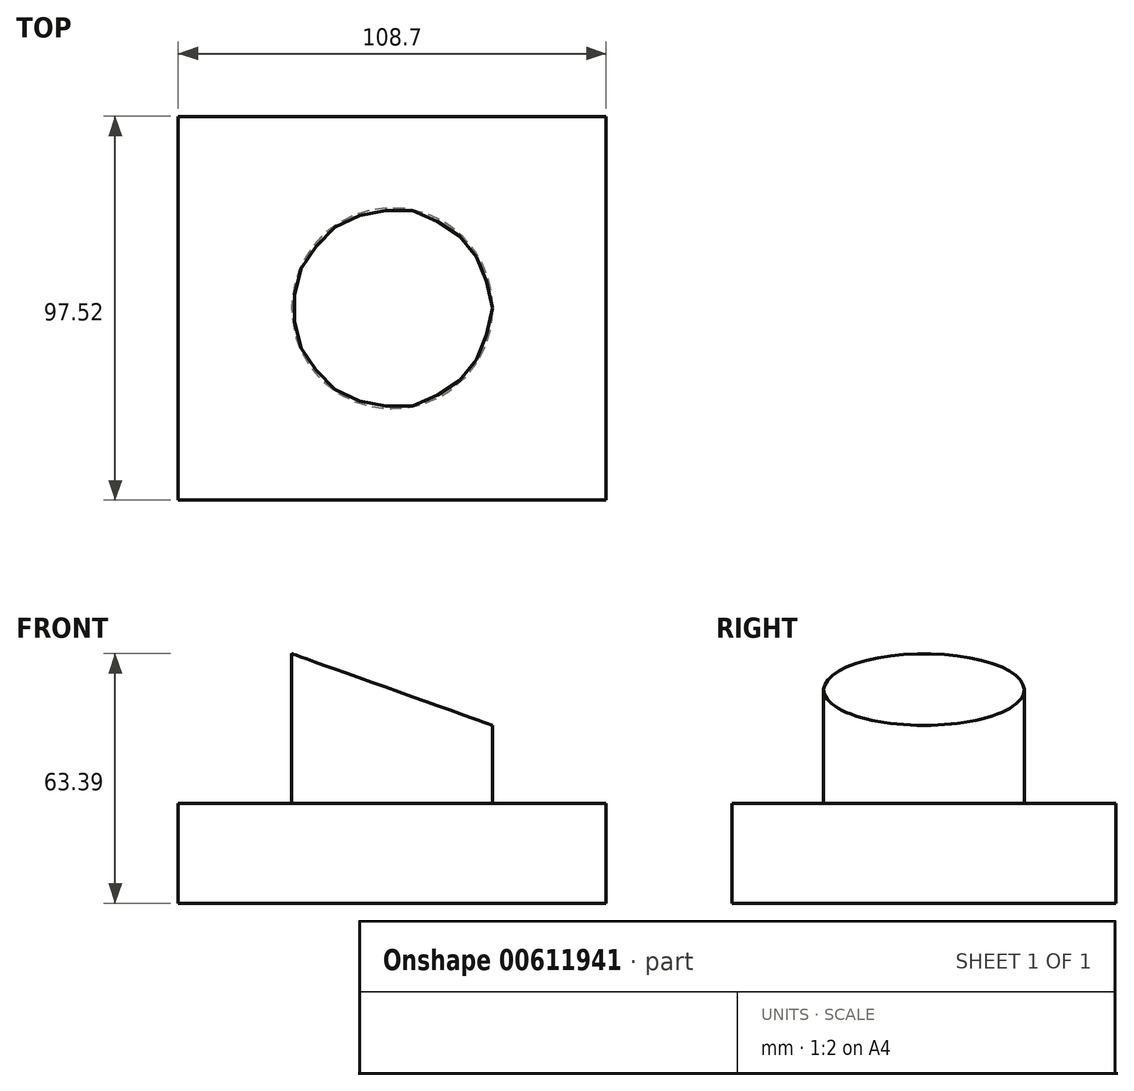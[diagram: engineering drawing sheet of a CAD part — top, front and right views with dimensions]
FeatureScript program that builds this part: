
annotation { "Feature Type Name" : "Feature", "Feature Type Description" : "" }
export const myFeature = defineFeature(function(context is Context, id is Id, definition is map)
    precondition{}
    {
        {
            var Q0;
            Q0=qCreatedBy(makeId("Top.planeOp"),FACE);
            var sketch = newSketch(context, id + "F0", { "sketchPlane" : qUnion([Q0])});
            skLineSegment(sketch, "E0.bottom", {"start": v(54.35, -48.76) * mm, "end": v(-54.35, -48.76) * mm});
            skLineSegment(sketch, "E0.top", {"start": v(54.35, 48.76) * mm, "end": v(-54.35, 48.76) * mm});
            skLineSegment(sketch, "E0.left", {"start": v(54.35, -48.76) * mm, "end": v(54.35, 48.76) * mm});
            skLineSegment(sketch, "E0.right", {"start": v(-54.35, -48.76) * mm, "end": v(-54.35, 48.76) * mm});
            skPoint(sketch, "E0.middle", {"position": v(0, 0) * mm});
            skSolve(sketch);
        }
        {
            var Q0;
            Q0=makeQuery(id+"F0.imprint","IMPRINT",FACE,{"disambiguationData":[TD([[makeQuery(id+"F0.imprint","IMPRINT",EDGE,{"derivedFrom":sQuery(id+"F0.wireOp",EDGE,"E0.bottom")}),-1.0]])]});
            extrude(context, id + "F1", {"entities" : qUnion([Q0]), "oppositeDirection" : true, "depth" : 25.4 * mm, "offsetDistance" : 25.4 * mm});
        }
        {
            var Q0;
            Q0=qCreatedBy(makeId("Top.planeOp"),FACE);
            var sketch = newSketch(context, id + "F2", { "sketchPlane" : qUnion([Q0])});
            skCircle(sketch, "E1", {"center": v(0, 0) * mm, "radius": 25.51 * mm});
            skSolve(sketch);
        }
        {
            var Q0;
            Q0=makeQuery(id+"F2.imprint","IMPRINT",FACE,{"disambiguationData":[TD([[makeQuery(id+"F2.imprint","IMPRINT",EDGE,{"derivedFrom":sQuery(id+"F2.wireOp",EDGE,"E1")}),1.0]])]});
            extrude(context, id + "F3", {"entities" : qUnion([Q0]), "operationType" : NewBodyOperationType.ADD, "depth" : 38.1 * mm, "offsetDistance" : 25.4 * mm});
        }
        {
            var Q0;
            Q0=qCreatedBy(makeId("Front.planeOp"),FACE);
            var sketch = newSketch(context, id + "F4", { "sketchPlane" : qUnion([Q0])});
            skLineSegment(sketch, "E2", {"start": v(-35.26, 41.47) * mm, "end": v(25.6, 19.72) * mm});
            skLineSegment(sketch, "E3", {"start": v(-35.26, 41.47) * mm, "end": v(25.86, 41.47) * mm});
            skLineSegment(sketch, "E4", {"start": v(25.86, 41.47) * mm, "end": v(25.6, 19.72) * mm});
            skSolve(sketch);
        }
        {
            var Q0;
            Q0 = qSketchRegion(id + "F4", true);
            var Q1;
            Q1=sQuery(id+"F4.wireOp",EDGE,"E2");
            var Q2;
            Q2=sQuery(id+"F4.wireOp",EDGE,"E3");
            var Q3;
            Q3=sQuery(id+"F4.wireOp",EDGE,"E4");
            extrude(context, id + "F5", {"entities" : qUnion([Q0]), "operationType" : NewBodyOperationType.REMOVE, "surfaceEntities" : qUnion([Q1, Q2, Q3]), "endBound" : BoundingType.SYMMETRIC, "depth" : 127 * mm, "offsetDistance" : 25.4 * mm});
        }
    });
